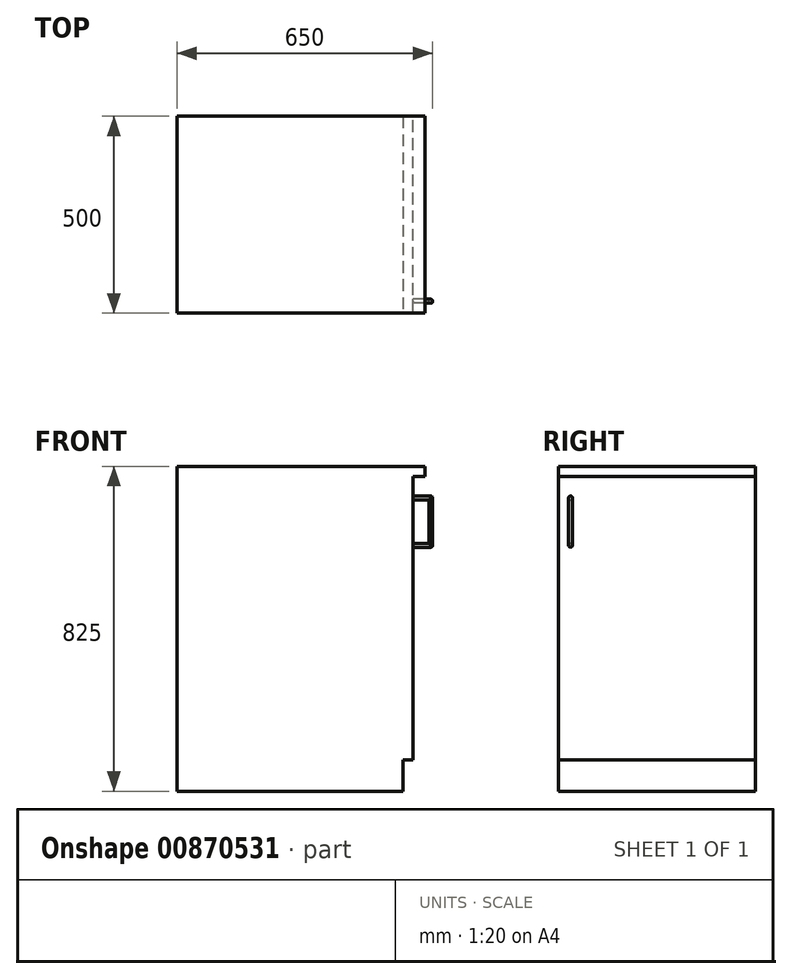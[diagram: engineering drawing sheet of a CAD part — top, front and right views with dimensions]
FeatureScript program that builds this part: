
annotation { "Feature Type Name" : "Feature", "Feature Type Description" : "" }
export const myFeature = defineFeature(function(context is Context, id is Id, definition is map)
    precondition{}
    {
        {
            var Q0;
            Q0=qCreatedBy(makeId("Top.planeOp"),FACE);
            var sketch = newSketch(context, id + "F0", { "sketchPlane" : qUnion([Q0])});
            skLineSegment(sketch, "E0.bottom", {"start": v(-300, 250) * mm, "end": v(300, 250) * mm});
            skLineSegment(sketch, "E0.top", {"start": v(-300, -250) * mm, "end": v(300, -250) * mm});
            skLineSegment(sketch, "E0.left", {"start": v(-300, 250) * mm, "end": v(-300, -250) * mm});
            skLineSegment(sketch, "E0.right", {"start": v(300, 250) * mm, "end": v(300, -250) * mm});
            skPoint(sketch, "E0.middle", {"position": v(0, 0) * mm});
            skSolve(sketch);
        }
        {
            var Q0;
            Q0=qSketchRegion(id+"F0",true);
            extrude(context, id + "F1", {"entities" : qUnion([Q0]), "depth" : 800 * mm, "offsetDistance" : 25 * mm});
        }
        {
            var Q0;
            Q0=makeQuery(id+"F1.opExtrude","SWEPT_FACE",FACE,{"disambiguationData":[OSD([sQuery(id+"F0.wireOp",EDGE,"E0.right")])]});
            var sketch = newSketch(context, id + "F2", { "sketchPlane" : qUnion([Q0])});
            skLineSegment(sketch, "E1.bottom", {"start": v(-250, 0) * mm, "end": v(250, 0) * mm});
            skLineSegment(sketch, "E1.top", {"start": v(-250, 80) * mm, "end": v(250, 80) * mm});
            skLineSegment(sketch, "E1.left", {"start": v(-250, 0) * mm, "end": v(-250, 80) * mm});
            skLineSegment(sketch, "E1.right", {"start": v(250, 0) * mm, "end": v(250, 80) * mm});
            skSolve(sketch);
        }
        {
            var Q0;
            Q0=qSketchRegion(id+"F2",true);
            extrude(context, id + "F3", {"entities" : qUnion([Q0]), "operationType" : NewBodyOperationType.REMOVE, "oppositeDirection" : true, "depth" : 25 * mm, "offsetDistance" : 25 * mm});
        }
        {
            var Q0;
            Q0=makeQuery(id+"F1.opExtrude","SWEPT_FACE",FACE,{"disambiguationData":[OSD([sQuery(id+"F0.wireOp",EDGE,"E0.right")])]});
            var sketch = newSketch(context, id + "F4", { "sketchPlane" : qUnion([Q0])});
            skLineSegment(sketch, "E2.bottom", {"start": v(-220, 750) * mm, "end": v(-220, 750) * mm});
            skLineSegment(sketch, "E2.top", {"start": v(-220, 620) * mm, "end": v(-220, 620) * mm});
            skLineSegment(sketch, "E2.left", {"start": v(-225, 745) * mm, "end": v(-225, 625) * mm});
            skLineSegment(sketch, "E2.right", {"start": v(-215, 745) * mm, "end": v(-215, 625) * mm});
            skPoint(sketch, "E3.visualSharp", {"position": v(-215, 750) * mm});
            skArc(sketch, "E3.filletArc", {"start": v(-215, 745) * mm, "mid": v(-216.46, 748.54) * mm, "end": v(-220, 750) * mm});
            skPoint(sketch, "E4.visualSharp", {"position": v(-215, 620) * mm});
            skArc(sketch, "E4.filletArc", {"start": v(-220, 620) * mm, "mid": v(-216.46, 621.46) * mm, "end": v(-215, 625) * mm});
            skPoint(sketch, "E5.visualSharp", {"position": v(-225, 620) * mm});
            skArc(sketch, "E5.filletArc", {"start": v(-225, 625) * mm, "mid": v(-223.54, 621.46) * mm, "end": v(-220, 620) * mm});
            skPoint(sketch, "E6.visualSharp", {"position": v(-225, 750) * mm});
            skArc(sketch, "E6.filletArc", {"start": v(-220, 750) * mm, "mid": v(-223.54, 748.54) * mm, "end": v(-225, 745) * mm});
            skSolve(sketch);
        }
        {
            var Q0;
            Q0=qSketchRegion(id+"F4",true);
            extrude(context, id + "F5", {"entities" : qUnion([Q0]), "operationType" : NewBodyOperationType.ADD, "depth" : 50 * mm, "offsetDistance" : 25 * mm});
        }
        {
            var Q0;
            Q0=makeQuery(id+"F5.opExtrude","CAP_FACE",FACE,{"disambiguationData":[OSD([sQuery(id+"F4.wireOp",EDGE,"E2.left"),sQuery(id+"F4.wireOp",EDGE,"E2.right"),sQuery(id+"F4.wireOp",EDGE,"E3.filletArc"),sQuery(id+"F4.wireOp",EDGE,"E4.filletArc"),sQuery(id+"F4.wireOp",EDGE,"E5.filletArc"),sQuery(id+"F4.wireOp",EDGE,"E6.filletArc")])],"isStart":false});
            fillet(context, id + "F6", {"entities" : qUnion([Q0]), "radius" : 5 * mm, "tangentPropagation" : true, "allowEdgeOverflow" : false});
        }
        {
            var Q0;
            Q0=makeQuery(id+"F5.opExtrude","SWEPT_FACE",FACE,{"disambiguationData":[OSD([sQuery(id+"F4.wireOp",EDGE,"E2.right")])]});
            var sketch = newSketch(context, id + "F7", { "sketchPlane" : qUnion([Q0])});
            skLineSegment(sketch, "E7.bottom", {"start": v(-340, 740) * mm, "end": v(-300, 740) * mm});
            skLineSegment(sketch, "E7.top", {"start": v(-340, 630) * mm, "end": v(-300, 630) * mm});
            skLineSegment(sketch, "E7.left", {"start": v(-340, 740) * mm, "end": v(-340, 630) * mm});
            skLineSegment(sketch, "E7.right", {"start": v(-300, 740) * mm, "end": v(-300, 630) * mm});
            skSolve(sketch);
        }
        {
            var Q0;
            Q0=makeQuery(id+"F7.imprint","IMPRINT",FACE,{"disambiguationData":[TD([[makeQuery(id+"F7.imprint","IMPRINT",EDGE,{"derivedFrom":sQuery(id+"F7.wireOp",EDGE,"E7.bottom")}),-1.0]])]});
            extrude(context, id + "F8", {"entities" : qUnion([Q0]), "operationType" : NewBodyOperationType.REMOVE, "oppositeDirection" : true, "depth" : 25 * mm, "offsetDistance" : 25 * mm});
        }
        {
            var Q0;
            Q0=makeQuery(id+"F8.boolean.opBoolean","COPY",EDGE,{"derivedFrom":makeQuery(id+"F8.opExtrude","CAP_EDGE",EDGE,{"disambiguationData":[OSD([sQuery(id+"F7.wireOp",EDGE,"E7.bottom")])],"isStart":true})});
            var Q1;
            Q1=makeQuery(id+"F8.boolean.opBoolean","COPY",EDGE,{"derivedFrom":makeQuery(id+"F8.opExtrude","CAP_EDGE",EDGE,{"disambiguationData":[OSD([sQuery(id+"F7.wireOp",EDGE,"E7.left")])],"isStart":true})});
            var Q2;
            Q2=makeQuery(id+"F8.boolean.opBoolean","COPY",EDGE,{"derivedFrom":makeQuery(id+"F8.opExtrude","CAP_EDGE",EDGE,{"disambiguationData":[OSD([sQuery(id+"F7.wireOp",EDGE,"E7.top")])],"isStart":true})});
            var Q3;
            Q3=makeQuery(id+"F8.boolean.opBoolean","INTERSECT",EDGE,{"derivedFrom":[makeQuery(id+"F5.opExtrude","SWEPT_FACE",FACE,{"disambiguationData":[OSD([sQuery(id+"F4.wireOp",EDGE,"E2.left")])]}),makeQuery(id+"F8.opExtrude","SWEPT_FACE",FACE,{"disambiguationData":[OSD([sQuery(id+"F7.wireOp",EDGE,"E7.bottom")])]})]});
            var Q4;
            Q4=makeQuery(id+"F8.boolean.opBoolean","INTERSECT",EDGE,{"derivedFrom":[makeQuery(id+"F5.opExtrude","SWEPT_FACE",FACE,{"disambiguationData":[OSD([sQuery(id+"F4.wireOp",EDGE,"E2.left")])]}),makeQuery(id+"F8.opExtrude","SWEPT_FACE",FACE,{"disambiguationData":[OSD([sQuery(id+"F7.wireOp",EDGE,"E7.left")])]})]});
            var Q5;
            Q5=makeQuery(id+"F8.boolean.opBoolean","INTERSECT",EDGE,{"derivedFrom":[makeQuery(id+"F5.opExtrude","SWEPT_FACE",FACE,{"disambiguationData":[OSD([sQuery(id+"F4.wireOp",EDGE,"E2.left")])]}),makeQuery(id+"F8.opExtrude","SWEPT_FACE",FACE,{"disambiguationData":[OSD([sQuery(id+"F7.wireOp",EDGE,"E7.top")])]})]});
            fillet(context, id + "F9", {"entities" : qUnion([Q0, Q1, Q2, Q3, Q4, Q5]), "radius" : 5 * mm, "tangentPropagation" : true, "allowEdgeOverflow" : false});
        }
        {
            var Q0;
            Q0=makeQuery(id+"F1.opExtrude","CAP_FACE",FACE,{"disambiguationData":[OSD([sQuery(id+"F0.wireOp",EDGE,"E0.bottom"),sQuery(id+"F0.wireOp",EDGE,"E0.top"),sQuery(id+"F0.wireOp",EDGE,"E0.left"),sQuery(id+"F0.wireOp",EDGE,"E0.right")])],"isStart":false});
            var sketch = newSketch(context, id + "F10", { "sketchPlane" : qUnion([Q0])});
            skLineSegment(sketch, "E8.bottom", {"start": v(-300, -250) * mm, "end": v(330, -250) * mm});
            skLineSegment(sketch, "E8.top", {"start": v(-300, 250) * mm, "end": v(330, 250) * mm});
            skLineSegment(sketch, "E8.left", {"start": v(-300, -250) * mm, "end": v(-300, 250) * mm});
            skLineSegment(sketch, "E8.right", {"start": v(330, -250) * mm, "end": v(330, 250) * mm});
            skSolve(sketch);
        }
        {
            var Q0;
            Q0=qSketchRegion(id+"F10",true);
            extrude(context, id + "F11", {"entities" : qUnion([Q0]), "operationType" : NewBodyOperationType.ADD, "depth" : 25 * mm, "offsetDistance" : 25 * mm});
        }
    });
